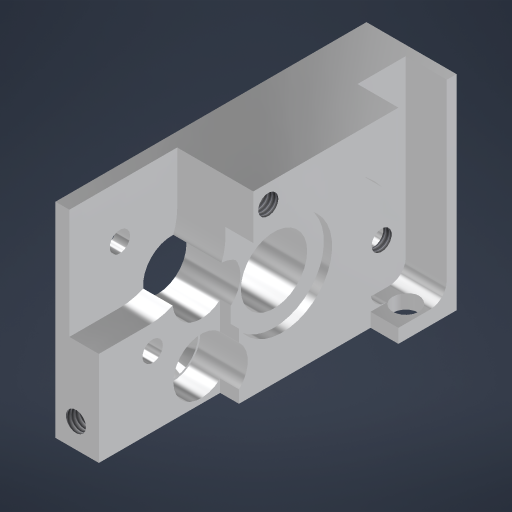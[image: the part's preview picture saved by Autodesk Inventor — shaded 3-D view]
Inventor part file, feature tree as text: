
AUTODESK INVENTOR PART (.ipt)
format: ipt  version: 2023 (Build 270158000, 158)  size: 485,888 bytes
history: native  units: mm
features: sketch x13, extrude x9, hole x9, projected_geometry x4, fillet x2, other x1
ambient origin geometry x8: Origin, YZ Plane, XZ Plane, XY Plane, X Axis, Y Axis, Z Axis, Center Point
bodies: Body1 (feature_tree)
feature tree (38):
  other  "Bryła1"
  extrude  "Wyciągnięcie proste1"  Depth=1.0mm
  sketch  "Szkic2"
  extrude  "Wyciągnięcie proste2"  Depth=1.0mm
  hole  "Otwór4"  [1 undecoded]
  hole  "Otwór1"  [1 undecoded]
  hole  "Otwór2"  [1 undecoded]
  hole  "Otwór3"  [1 undecoded]
  hole  "Otwór5"  [1 undecoded]
  hole  "Otwór6"  [1 undecoded]
  extrude  "Wyciągnięcie proste3"  Depth=10.0mm
  hole  "Otwór7"  [1 undecoded]
  extrude  "Wyciągnięcie proste4"  Depth=1.0mm TaperAngle=0.0deg
  hole  "Otwór8"  [1 undecoded]
  hole  "Otwór9"  [1 undecoded]
  extrude  "Wyciągnięcie proste5"  TaperAngle=0.0deg  [1 undecoded]
  fillet  "Zaokrąglenie1"  Radius=8.5mm
  extrude  "Wyciągnięcie proste6"  TaperAngle=0.0deg  [1 undecoded]
  extrude  "Wyciągnięcie proste9"  TaperAngle=0.0deg  [1 undecoded]
  extrude  "Wyciągnięcie proste10"  Depth=1.0mm
  fillet  "Zaokrąglenie2"  Radius=23.0mm
  extrude  "Extrusion11"  Depth=1.0mm
  sketch  "Szkic1"
  sketch  "Szkic3"
  sketch  "Szkic4"
  sketch  "Szkic5"
  sketch  "Szkic6"
  sketch  "Szkic7"
  sketch  "Szkic8"
  sketch  "Szkic9"
  sketch  "Szkic10"
  projected_geometry  "Pętla rzutowana1"
  projected_geometry  "Pętla rzutowana3"
  sketch  "Szkic13"
  projected_geometry  "Pętla rzutowana4"
  sketch  "Szkic14"
  projected_geometry  "Pętla rzutowana5"
  sketch  "Sketch15"  dims[d3=0.0mm d4=7.0mm d5=12.5mm d6=12.5mm d7=2.5mm d8=8.1mm d9=11.0mm d10=20.1mm d12=8.75mm d13=10.0mm d14=13.75mm d15=11.0mm d16=0.0mm d17=14.0mm d18=6.0mm d19=4.0mm d20=2.0mm d21=90.0deg d23=0.0mm d24=16.5mm d25=6.0mm d26=4.0mm d27=2.0mm d28=90.0deg d30=0.0mm d31=22.0mm d32=6.0mm d33=4.0mm d34=2.0mm d35=90.0deg d36=3.4mm d37=0.0mm d38=8.5mm d39=6.8mm d40=6.0mm d41=4.0mm d42=2.0mm d43=90.0deg d44=9.2mm d45=0.0mm d46=3.4mm d47=6.0mm d48=6.3mm d49=2.0mm d50=90.0deg d51=9.2mm d52=0.0mm d54=7.0mm d55=23.0mm d56=2.3mm d57=2.459mm d58=6.0mm d59=6.3mm d60=2.0mm d61=90.0deg d62=8.8mm d63=20.594885mm d64=1.7mm d65=33.85mm d66=5.9mm d67=5.0mm d68=0.0mm d69=2.5mm d70=3.0mm d71=2.459mm d72=4.5mm d73=6.3mm d74=2.0mm d75=90.0deg d76=5.0mm d77=20.594885mm d78=5.0mm d79=0.0mm d80=3.2mm d81=4.5mm d82=6.3mm d83=2.0mm d84=90.0deg d85=5.0mm d86=20.594885mm d87=2.5mm d88=11.0mm d89=21.0mm d90=2.459mm d91=5.7mm d92=6.3mm d93=2.0mm d94=14.7mm d95=6.0mm d96=20.594885mm d97=4.0mm d98=20.0mm d99=2.0mm d100=0.0mm d101=2.0mm d102=17.500416mm d103=10.0mm d104=0.0mm d111=10.0mm d112=0.0mm d114=2.0mm d115=10.0mm d116=0.0mm d117=2.0mm d118=12.2mm d119=1.0mm d120=0.0mm]
note: 12 required parameter values undecoded (feature->parameter linkage not recoverable at this tier; creation-order binding heuristic only, values carry confidence <= 0.55)
